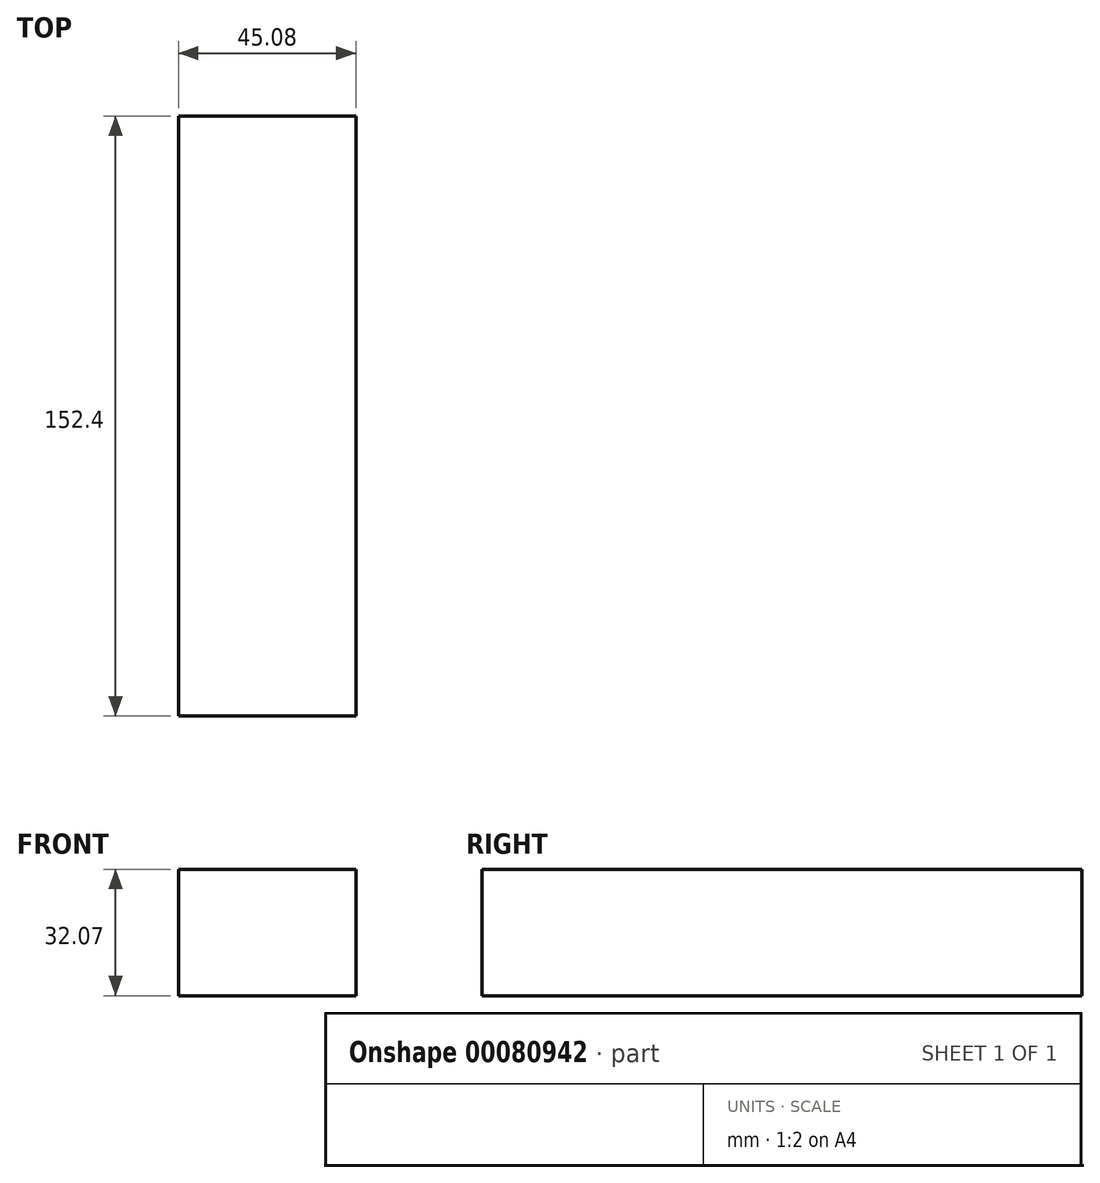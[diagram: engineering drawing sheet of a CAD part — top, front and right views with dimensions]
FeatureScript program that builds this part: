
annotation { "Feature Type Name" : "Feature", "Feature Type Description" : "" }
export const myFeature = defineFeature(function(context is Context, id is Id, definition is map)
    precondition{}
    {
        {
            var Q0;
            Q0=qCreatedBy(makeId("Front.planeOp"),FACE);
            var sketch = newSketch(context, id + "F0", { "sketchPlane" : qUnion([Q0])});
            skLineSegment(sketch, "E0.bottom", {"start": v(-60, 51.42) * mm, "end": v(-14.93, 51.42) * mm});
            skLineSegment(sketch, "E0.top", {"start": v(-60, 19.35) * mm, "end": v(-14.93, 19.35) * mm});
            skLineSegment(sketch, "E0.left", {"start": v(-60, 51.42) * mm, "end": v(-60, 19.35) * mm});
            skLineSegment(sketch, "E0.right", {"start": v(-14.93, 51.42) * mm, "end": v(-14.93, 19.35) * mm});
            skSolve(sketch);
        }
        {
            var Q0;
            Q0=makeQuery(id+"F0.imprint","IMPRINT",FACE,{"disambiguationData":[TD([[makeQuery(id+"F0.imprint","IMPRINT",EDGE,{"derivedFrom":sQuery(id+"F0.wireOp",EDGE,"E0.bottom")}),-1.0]])]});
            extrude(context, id + "F1", {"entities" : qUnion([Q0]), "oppositeDirection" : true, "depth" : 152.4 * mm});
        }
    });
